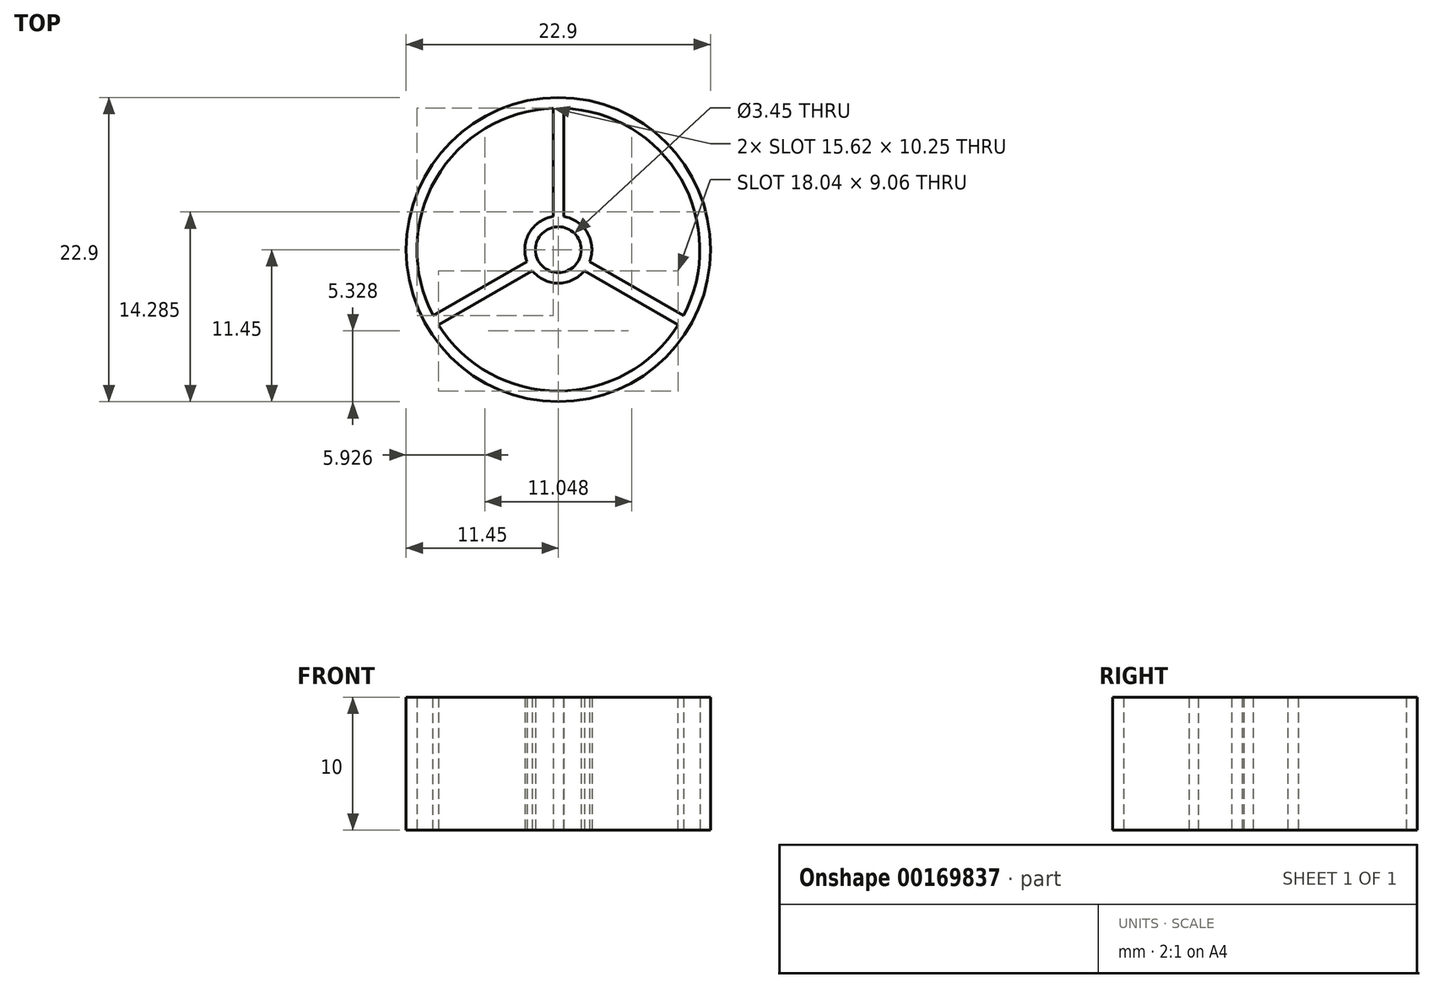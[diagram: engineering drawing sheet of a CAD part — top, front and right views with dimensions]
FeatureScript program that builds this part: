
annotation { "Feature Type Name" : "Feature", "Feature Type Description" : "" }
export const myFeature = defineFeature(function(context is Context, id is Id, definition is map)
    precondition{}
    {
        {
            var Q0;
            Q0=qCreatedBy(makeId("Front.planeOp"),FACE);
            var sketch = newSketch(context, id + "F0", { "sketchPlane" : qUnion([Q0])});
            skLineSegment(sketch, "E0.bottom", {"start": v(-11.45, 0) * mm, "end": v(-10.65, 0) * mm});
            skLineSegment(sketch, "E0.top", {"start": v(-11.45, 10) * mm, "end": v(-10.65, 10) * mm});
            skLineSegment(sketch, "E0.left", {"start": v(-11.45, 0) * mm, "end": v(-11.45, 10) * mm});
            skLineSegment(sketch, "E0.right", {"start": v(-10.65, 0) * mm, "end": v(-10.65, 10) * mm});
            skLineSegment(sketch, "E1.bottom", {"start": v(-2.53, 0) * mm, "end": v(-1.72, 0) * mm});
            skLineSegment(sketch, "E1.top", {"start": v(-2.53, 10) * mm, "end": v(-1.73, 10) * mm});
            skLineSegment(sketch, "E1.left", {"start": v(-2.53, 0) * mm, "end": v(-2.53, 10) * mm});
            skLineSegment(sketch, "E1.right", {"start": v(-1.73, 0) * mm, "end": v(-1.73, 10) * mm});
            skLineSegment(sketch, "E2", {"start": v(0, 0) * mm, "end": v(0, 10) * mm});
            skSolve(sketch);
        }
        {
            var Q0;
            Q0 = qSketchRegion(id + "F0", true);
            var Q1;
            Q1=sQuery(id+"F0.wireOp",EDGE,"E2");
            revolve(context, id + "F1", {"entities" : qUnion([Q0]), "axis" : qUnion([Q1]), "revolveType" : RevolveType.FULL});
        }
        {
            var Q0;
            Q0=qCreatedBy(makeId("Top.planeOp"),FACE);
            var sketch = newSketch(context, id + "F2", { "sketchPlane" : qUnion([Q0])});
            skCircle(sketch, "E3.0", {"center": v(0, 0) * mm, "radius": 10.65 * mm, "construction": true});
            skCircle(sketch, "E4.0", {"center": v(0, 0) * mm, "radius": 1.73 * mm, "construction": true});
            skLineSegment(sketch, "E5.bottom", {"start": v(-0.4, 10.65) * mm, "end": v(0.4, 10.65) * mm});
            skLineSegment(sketch, "E5.top", {"start": v(-0.4, 1.73) * mm, "end": v(0.4, 1.73) * mm});
            skLineSegment(sketch, "E5.left", {"start": v(-0.4, 10.65) * mm, "end": v(-0.4, 1.73) * mm});
            skLineSegment(sketch, "E5.right", {"start": v(0.4, 10.65) * mm, "end": v(0.4, 1.73) * mm});
            skPoint(sketch, "E6", {"position": v(0, 1.73) * mm});
            skCircle(sketch, "E7.1.1", {"center": v(0, 0) * mm, "radius": 11.05 * mm, "construction": true});
            skCircle(sketch, "E7.2.1", {"center": v(0, 0) * mm, "radius": 11.05 * mm, "construction": true});
            skLineSegment(sketch, "E8.1.0", {"start": v(-1.3, -1.2) * mm, "end": v(-1.7, -0.52) * mm});
            skLineSegment(sketch, "E8.1.1", {"start": v(-9.02, -5.67) * mm, "end": v(-1.3, -1.2) * mm});
            skLineSegment(sketch, "E8.1.2", {"start": v(-9.42, -4.98) * mm, "end": v(-1.7, -0.52) * mm});
            skLineSegment(sketch, "E8.1.3", {"start": v(-9.02, -5.67) * mm, "end": v(-9.42, -4.98) * mm});
            skLineSegment(sketch, "E8.2.0", {"start": v(1.7, -0.52) * mm, "end": v(1.3, -1.2) * mm});
            skLineSegment(sketch, "E8.2.1", {"start": v(9.42, -4.98) * mm, "end": v(1.7, -0.52) * mm});
            skLineSegment(sketch, "E8.2.2", {"start": v(9.02, -5.67) * mm, "end": v(1.3, -1.2) * mm});
            skLineSegment(sketch, "E8.2.3", {"start": v(9.42, -4.98) * mm, "end": v(9.02, -5.67) * mm});
            skSolve(sketch);
        }
        {
            var Q0;
            Q0 = qSketchRegion(id + "F2", true);
            var Q1;
            Q1=makeQuery(id+"F1.opRevolve","SWEPT_FACE",FACE,{"disambiguationData":[OSD([sQuery(id+"F0.wireOp",EDGE,"E1.top")])]});
            extrude(context, id + "F3", {"entities" : qUnion([Q0]), "operationType" : NewBodyOperationType.ADD, "endBound" : BoundingType.UP_TO_SURFACE, "endBoundEntityFace" : qUnion([Q1]), "depth" : 25 * mm});
        }
    });
